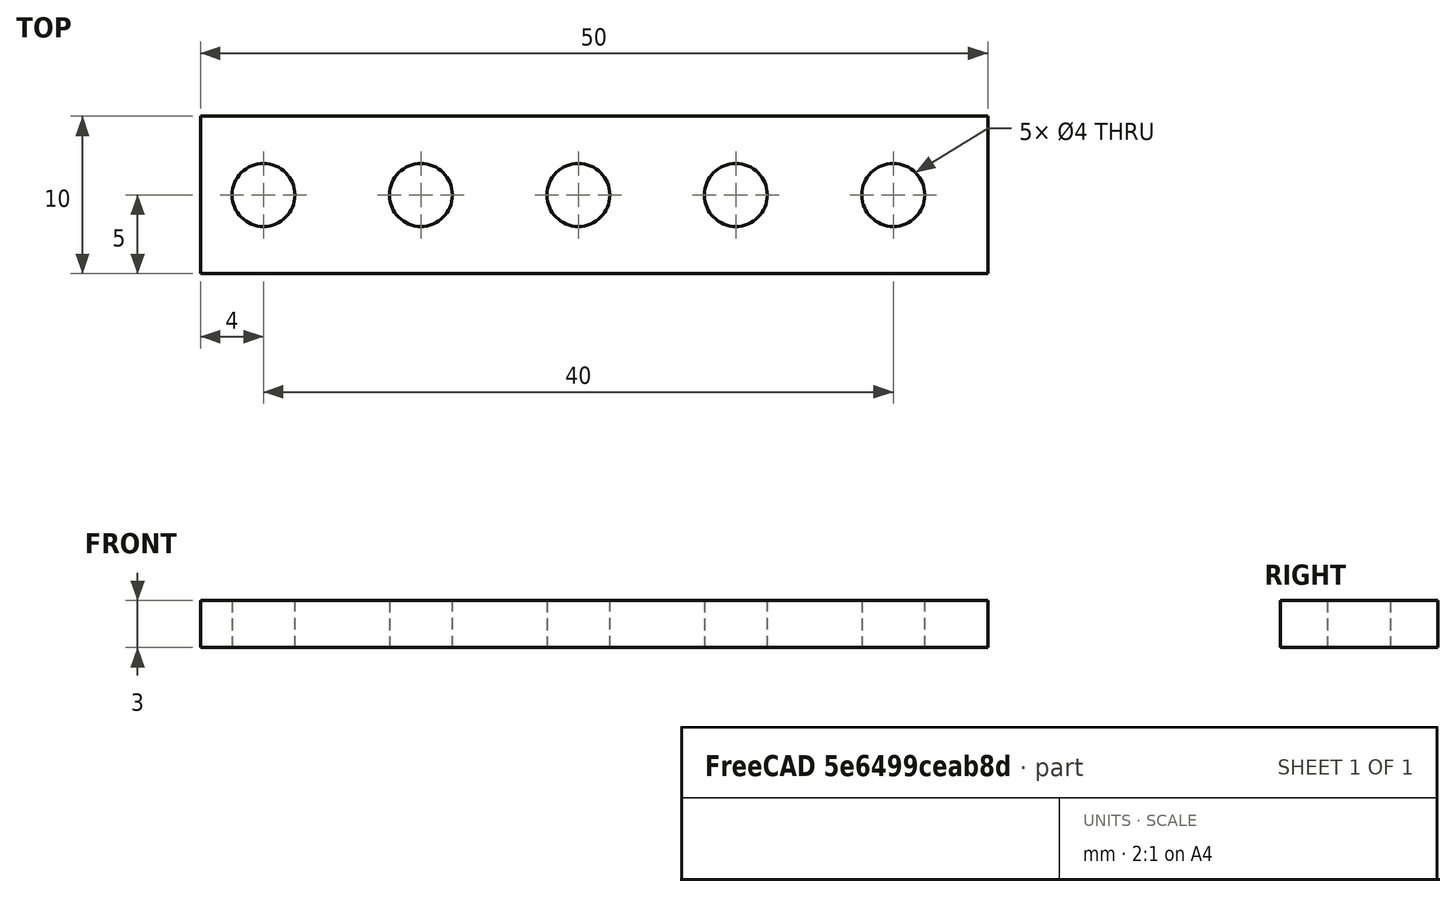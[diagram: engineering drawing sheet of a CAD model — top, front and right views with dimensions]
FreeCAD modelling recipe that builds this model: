
FCSTD DOCUMENT  (FreeCAD 1.0R38806 (Git))
Label: reto_3
License: All rights reserved
LicenseURL: https://en.wikipedia.org/wiki/All_rights_reserved
objects: Part::Cylinder×5, Part::Cut×5, Part::Box×1
note: 11 computed .brp shape members not serialized (recipe doc carries the construction recipe); baked Part::Feature solids carry a one-line shape summary decoded from their .brp

FEATURE [Part::Box] Box  label="Cube"
  AttacherType = Attacher::AttachEngine3D
  Height = 3
  Length = 50
  Width = 10
FEATURE [Part::Cylinder] Cylinder
  Angle = 360
  AttacherType = Attacher::AttachEngine3D
  FirstAngle = 0
  Height = 10
  Placement = pos=(4,5,-3) rot=(0,0,1;0rad)
  Radius = 2
  SecondAngle = 0
FEATURE [Part::Cylinder] Cylinder001 .. Cylinder004  x4 (patterned run collapsed; names and placements below)
  Angle = 360
  AttacherType = Attacher::AttachEngine3D
  FirstAngle = 0
  Height = 10
  Radius = 2
  SecondAngle = 0
  placements: 4 in arithmetic series — first pos=(14,5,-3) rot=(0,0,1;0rad), step (10,0,0), last pos=(44,5,-3) rot=(0,0,1;0rad)
FEATURE [Part::Cut] Cut
  Base = -> Box
  Refine = true
  Tool = -> Cylinder
FEATURE [Part::Cut] Cut001
  Base = -> Cut
  Refine = true
  Tool = -> Cylinder001
FEATURE [Part::Cut] Cut002
  Base = -> Cut001
  Refine = true
  Tool = -> Cylinder002
FEATURE [Part::Cut] Cut003
  Base = -> Cut002
  Refine = true
  Tool = -> Cylinder003
FEATURE [Part::Cut] Cut004
  Base = -> Cut003
  Refine = true
  Tool = -> Cylinder004
